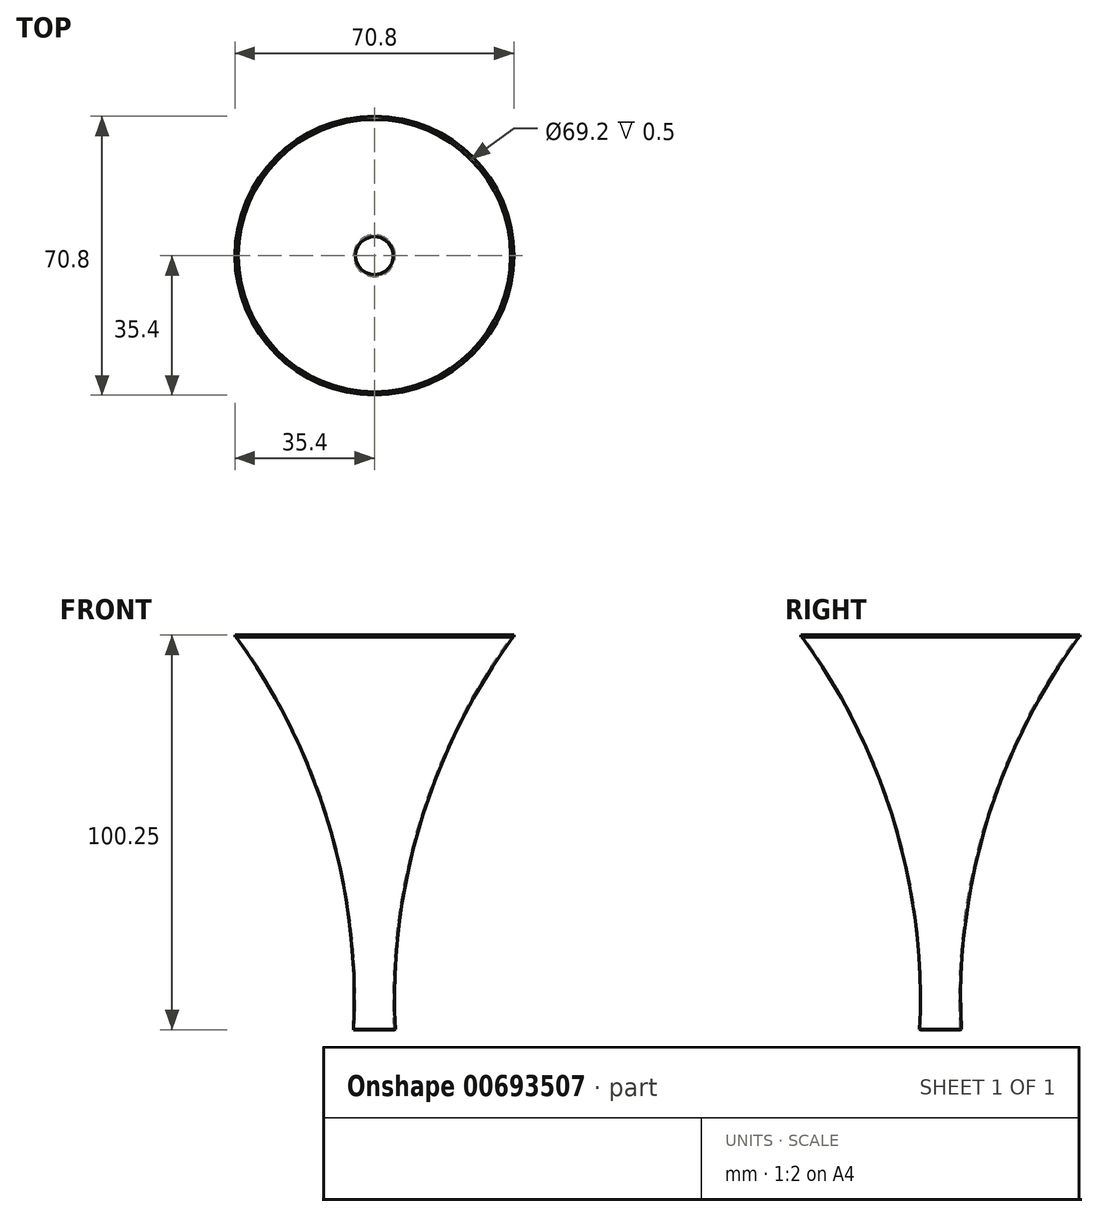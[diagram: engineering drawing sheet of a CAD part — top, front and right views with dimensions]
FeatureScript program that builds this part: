
annotation { "Feature Type Name" : "Feature", "Feature Type Description" : "" }
export const myFeature = defineFeature(function(context is Context, id is Id, definition is map)
    precondition{}
    {
        {
            var Q0;
            Q0=qCreatedBy(makeId("Top.planeOp"),FACE);
            var sketch = newSketch(context, id + "F0", { "sketchPlane" : qUnion([Q0])});
            skCircle(sketch, "E0", {"center": v(0, 0) * mm, "radius": 5 * mm});
            skSolve(sketch);
        }
        {
            var Q0;
            Q0=qCreatedBy(makeId("Right.planeOp"),FACE);
            var sketch = newSketch(context, id + "F1", { "sketchPlane" : qUnion([Q0])});
            skLineSegment(sketch, "E1", {"start": v(0, 0) * mm, "end": v(0, 100) * mm});
            skLineSegment(sketch, "E2", {"start": v(0, 100) * mm, "end": v(35, 100) * mm});
            skLineSegment(sketch, "E3", {"start": v(0, 100) * mm, "end": v(-35, 100) * mm});
            skLineSegment(sketch, "E4", {"start": v(0, 0) * mm, "end": v(5, 0) * mm});
            skLineSegment(sketch, "E5", {"start": v(0, 0) * mm, "end": v(-5, 0) * mm});
            skArc(sketch, "E6", {"start": v(-5, 0) * mm, "mid": v(-11.41, 52.58) * mm, "end": v(-35, 100) * mm});
            skArc(sketch, "E7.0", {"start": v(-5.3, 0.01) * mm, "mid": v(-11.7, 52.49) * mm, "end": v(-35.24, 99.82) * mm});
            skLineSegment(sketch, "E8", {"start": v(-5, 0) * mm, "end": v(-5.3, 0.01) * mm});
            skLineSegment(sketch, "E9", {"start": v(-35, 100) * mm, "end": v(-35.24, 99.82) * mm});
            skLineSegment(sketch, "E10.bottom", {"start": v(35.4, 100.25) * mm, "end": v(34.6, 100.25) * mm});
            skLineSegment(sketch, "E10.top", {"start": v(35.4, 99.75) * mm, "end": v(34.6, 99.75) * mm});
            skLineSegment(sketch, "E10.left", {"start": v(35.4, 100.25) * mm, "end": v(35.4, 99.75) * mm});
            skLineSegment(sketch, "E10.right", {"start": v(34.6, 100.25) * mm, "end": v(34.6, 99.75) * mm});
            skPoint(sketch, "E10.middle", {"position": v(35, 100) * mm});
            skSolve(sketch);
        }
        {
            var Q0;
            Q0=makeQuery(id+"F1.imprint","IMPRINT",FACE,{"disambiguationData":[TD([[makeQuery(id+"F1.imprint","IMPRINT",EDGE,{"derivedFrom":sQuery(id+"F1.wireOp",EDGE,"E6")}),1.0]])]});
            var Q1;
            Q1=sQuery(id+"F1.wireOp",EDGE,"E1");
            revolve(context, id + "F2", {"entities" : qUnion([Q0]), "axis" : qUnion([Q1]), "revolveType" : RevolveType.FULL});
        }
        {
            var Q0;
            {var subQ0=sQuery(id+"F1.wireOp",EDGE,"E10.bottom");Q0=makeQuery(id+"F1.imprint","IMPRINT",FACE,{"disambiguationData":[TD([[makeQuery(id+"F1.imprint","IMPRINT",EDGE,{"derivedFrom":subQ0}),1.0]])]});}
            var Q1;
            Q1=sQuery(id+"F1.wireOp",EDGE,"E1");
            revolve(context, id + "F3", {"operationType" : NewBodyOperationType.ADD, "entities" : qUnion([Q0]), "axis" : qUnion([Q1]), "revolveType" : RevolveType.FULL});
        }
    });
